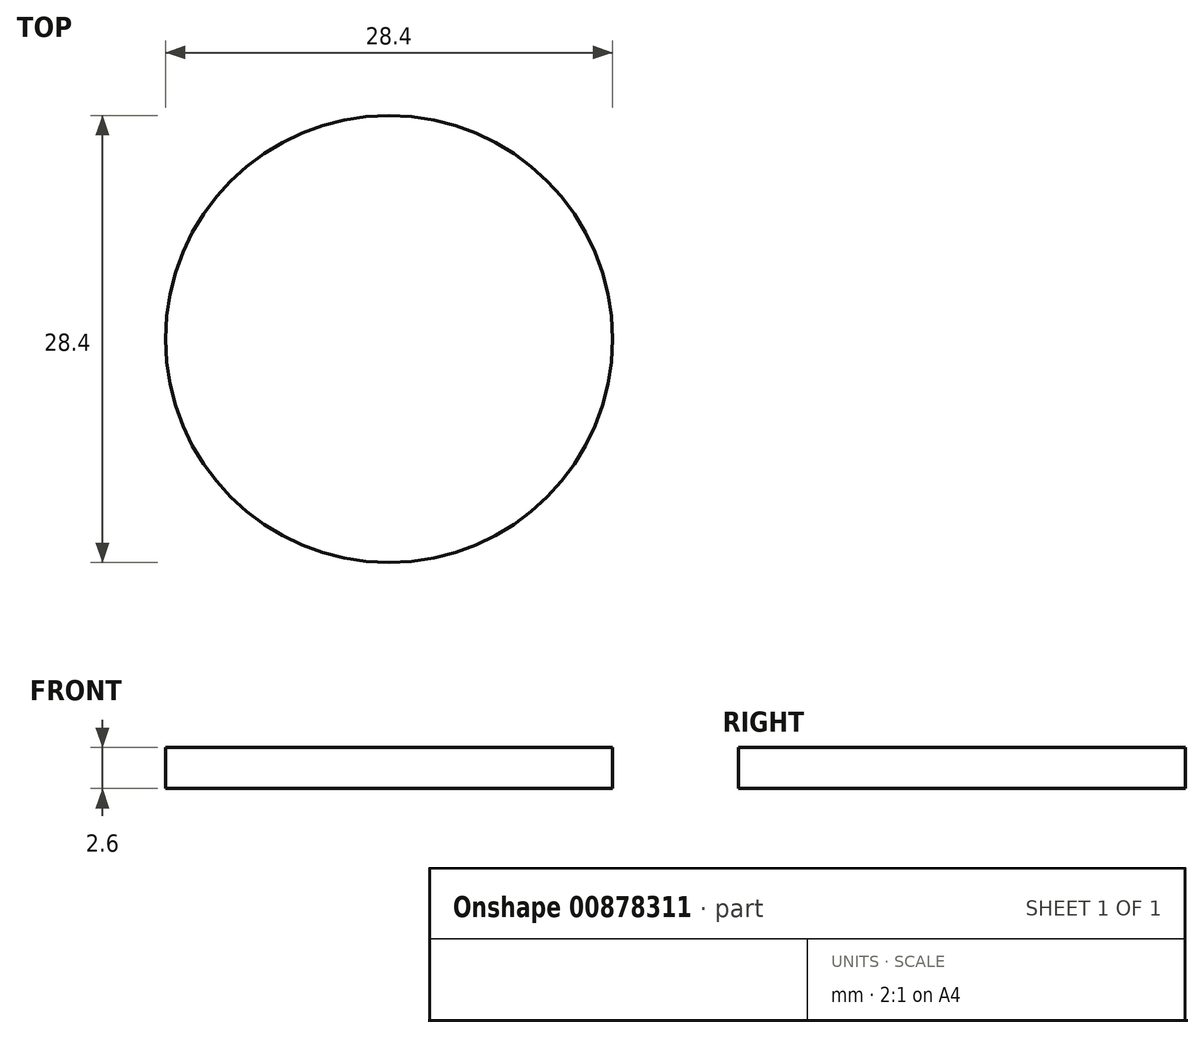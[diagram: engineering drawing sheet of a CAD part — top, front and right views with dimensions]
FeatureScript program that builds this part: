
annotation { "Feature Type Name" : "Feature", "Feature Type Description" : "" }
export const myFeature = defineFeature(function(context is Context, id is Id, definition is map)
    precondition{}
    {
        {
            var Q0;
            Q0=qCreatedBy(makeId("Top.planeOp"),FACE);
            var sketch = newSketch(context, id + "F0", { "sketchPlane" : qUnion([Q0])});
            skCircle(sketch, "E0", {"center": v(7.55, -23.24) * mm, "radius": 14.2 * mm});
            skSolve(sketch);
        }
        {
            var Q0;
            Q0=makeQuery(id+"F0.imprint","IMPRINT",FACE,{"disambiguationData":[TD([[makeQuery(id+"F0.imprint","IMPRINT",EDGE,{"derivedFrom":sQuery(id+"F0.wireOp",EDGE,"E0")}),1.0]])]});
            extrude(context, id + "F1", {"entities" : qUnion([Q0]), "depth" : 2.6 * mm, "offsetDistance" : 25 * mm});
        }
    });
